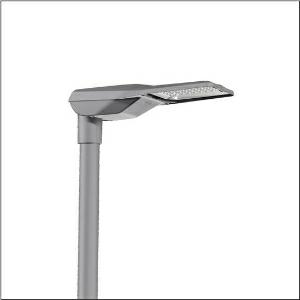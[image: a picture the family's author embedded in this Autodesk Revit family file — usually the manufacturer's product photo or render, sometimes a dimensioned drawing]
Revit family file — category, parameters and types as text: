
# Revit family: streetlight_sl_21_iq_mini___p0_8a_5xe2u31d08jb_69dd
name_source: partatom
category: Lighting Fixtures
units: mm (PartAtom-declared; Revit-internal decimal feet)

## family parameters
Cut with Voids When Loaded = No
Host = Face
Light Source = No
Part Type = Normal
Room Calculation Point = No
Round Connector Dimension = Use Diameter
Shared = No

## types (1)
- --- (1 x LED, 10920 lm, 71.6 W, 3000K)
    Apparent Load = 72 VA
    CIE Flux Codes = 36 69 97 100 100
    Color Rendering = 70
    Color Temperature = 3000K
    Default Elevation = 1800 mm
    Description = Streetlight SL 21 iQ mini, mast luminaire, primary light control with lens, of PMMA, primary optical cover: cover, of toughened safety glass, transparent, light distribution: P0.8a, light emission: direct distribution, primary light characteristic: asymmetric, installation type: post-top, side-entry, LED, High Power LED, rated luminous flux: 10.920lm, luminous efficacy: 153lm/W, light colour: 730, colour temperature: 3000K, control gear: iQ-Comfort, control: pre-setting: linear dimming characteristic, Auto-Match, Temp-Guard, Lumen-Switch, Night-Set, Smart-Wire, Light-Fading, Desk-Remote (wireless, voltage-free reading and setting of iQ features in the workshop via application-optimized NFC function/RFID function), optimised constant luminous flux control (CLO 2.0), mains connection: 220..240V, AC, 50/60Hz, start of lifetime: 72W, end of service life: 75W, reduction: 33W, luminaire housing, of diecast aluminium, powder-coated, Siteco® metallic grey (DB 702S), corrosivity category C5 mid according to DIN EN ISO 12944, please order mast flange separately, inclination adjustable: 0°, 5°, 10°, 15°, sealing non-destructively replaceable, multi-level sealing system, length: 628mm, width: 235mm, height: 110mm, mast flange for spigot size: 42mm (side-entry): 5XC10008XM4, 60/48mm (side-entry/post-top): 5XC10108XM2, 76/60mm (side-entry/post-top): 5XC10108XM1, mounting height: 4..8m, protection rating (complete): IP66, insulation class (complete): insulation class II (safety insulation), certification: CE, ENEC, ENEC+, VDE, impact resistance: IK10, permissible operating ambient temperature for outdoor applications: -40..+50°C, standard-compliant lighting for roads and squares, packaging unit: 1 piece

Light Distribution: P0.8a
    Height = 110 mm
    Lamp = 1 x LED
    Lamp Light Flux = 10920 lm
    Lamp Power = 71.6 W
    Lamp count = 1
    Length = 625 mm
    Luminous efficacy = 153 lm/W
    Manufacturer = Siteco
    ModVariant = No
    Model = 5XE2U31D08JB
    Number of Poles = 1
    OnlyDefault = Yes
    Power Factor = 1
    Product Name = Streetlight SL 21 iQ mini | P0.8a
    Product group = mast luminaire | pylon top
    ProductGroupID = 6100
    Protection Class = Protection class II
    Protection Degree = IP 66
    RLX_Detail_Level = 1
    RLX_Emergency_Light_Flux = 0 lm
    RLX_Emergency_Type = 0
    RLX_Emergency_Type_DB = No
    RlxData = <blob elided: 92277 chars, md5=f3355b99>
    Socket = socket
    Standby Power = 0 W
    System Light Flux = 10920 lm
    System Power = 72 W
    Type Comments = factory setting: luminous flux: 100 % | dim-lin: 254 | 746 mA
    Type Image = l_1003519.jpg
    URL = http://relux.com
    VarID = @adj_093157
    Voltage = 0 V
    Weight = 0.00 kg
    Width = 234 mm

## geometry (parser evidence)
native form markers: Blend x4, Sweep x12
no freeform markers — native parametric forms only
